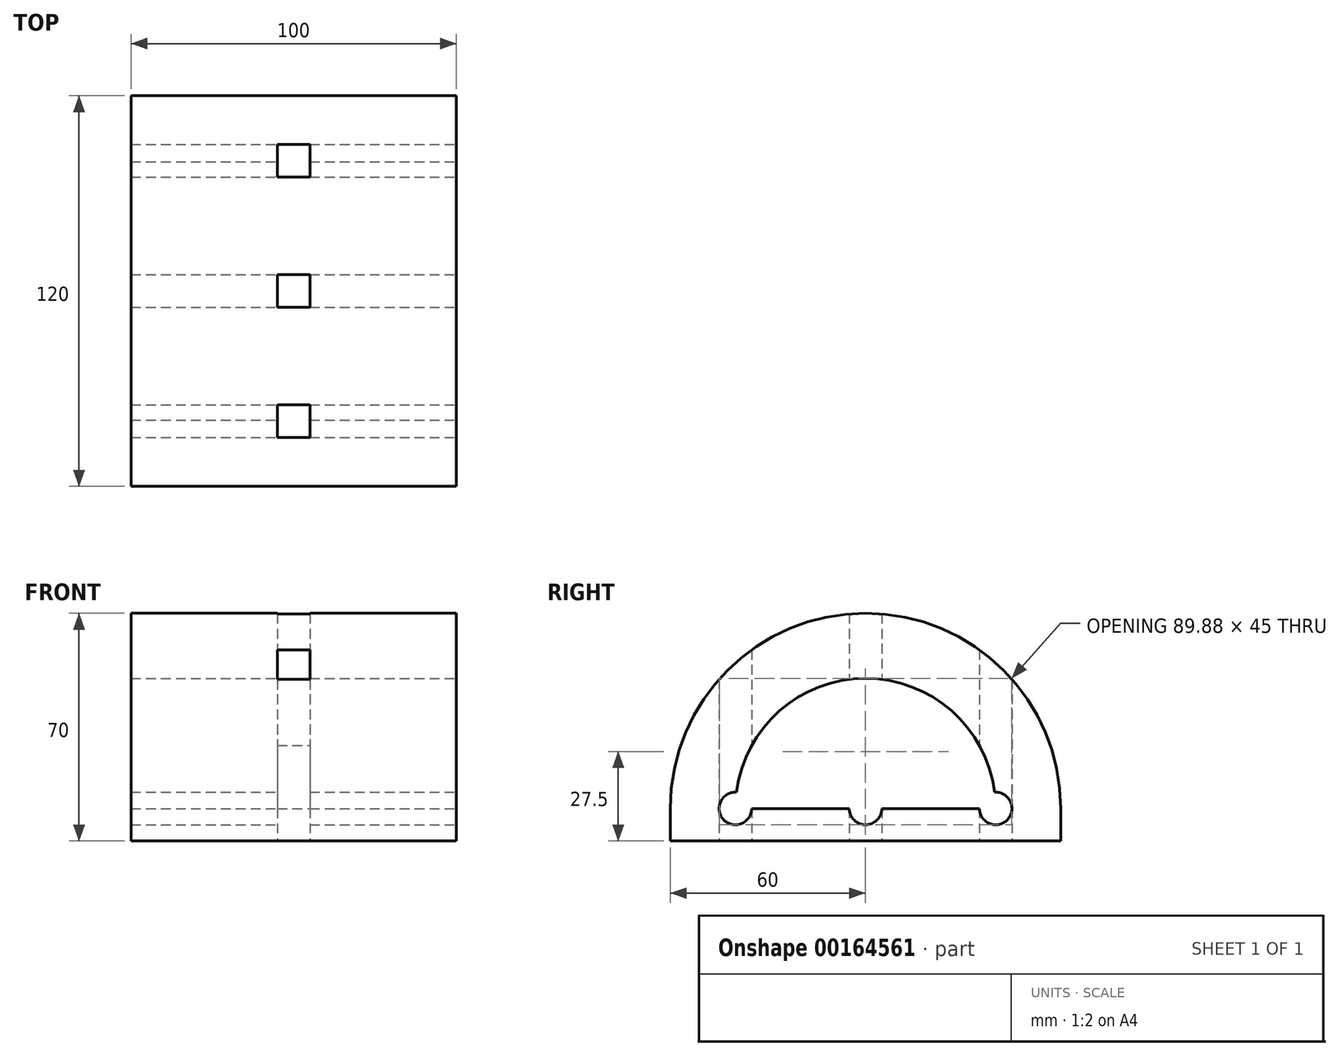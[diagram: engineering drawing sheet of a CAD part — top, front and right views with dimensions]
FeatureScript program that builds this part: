
annotation { "Feature Type Name" : "Feature", "Feature Type Description" : "" }
export const myFeature = defineFeature(function(context is Context, id is Id, definition is map)
    precondition{}
    {
        {
            var Q0;
            Q0=qCreatedBy(makeId("Right.planeOp"),FACE);
            var sketch = newSketch(context, id + "F0", { "sketchPlane" : qUnion([Q0])});
            skLineSegment(sketch, "E0.top", {"start": v(60, 10) * mm, "end": v(-60, 10) * mm});
            skLineSegment(sketch, "E0.left", {"start": v(60, 0) * mm, "end": v(60, 10) * mm});
            skLineSegment(sketch, "E0.right", {"start": v(-60, 0) * mm, "end": v(-60, 10) * mm});
            skPoint(sketch, "E0.middle", {"position": v(0, 0) * mm});
            skLineSegment(sketch, "E1", {"start": v(-60, 0) * mm, "end": v(60, 0) * mm});
            skArc(sketch, "E2", {"start": v(60, 10) * mm, "mid": v(0, 70) * mm, "end": v(-60, 10) * mm});
            skSolve(sketch);
        }
        {
            var Q0;
            Q0 = qSketchRegion(id + "F0", true);
            extrude(context, id + "F1", {"entities" : qUnion([Q0]), "depth" : 100 * mm});
        }
        {
            var Q0;
            Q0=makeQuery(id+"F1.opExtrude","CAP_FACE",FACE,{"disambiguationData":[OSD([sQuery(id+"F0.wireOp",EDGE,"E0.left"),sQuery(id+"F0.wireOp",EDGE,"E0.right"),sQuery(id+"F0.wireOp",EDGE,"E1"),sQuery(id+"F0.wireOp",EDGE,"E2")])],"isStart":false});
            var sketch = newSketch(context, id + "F2", { "sketchPlane" : qUnion([Q0])});
            skLineSegment(sketch, "E3", {"start": v(-40, 10) * mm, "end": v(40, 10) * mm});
            skArc(sketch, "E4", {"start": v(40, 10) * mm, "mid": v(0, 50) * mm, "end": v(-40, 10) * mm});
            skSolve(sketch);
        }
        {
            var Q0;
            Q0 = qSketchRegion(id + "F2", true);
            extrude(context, id + "F3", {"entities" : qUnion([Q0]), "operationType" : NewBodyOperationType.REMOVE, "endBound" : BoundingType.THROUGH_ALL, "oppositeDirection" : true, "depth" : 25 * mm});
        }
        {
            var Q0;
            Q0=makeQuery(id+"F1.opExtrude","CAP_FACE",FACE,{"disambiguationData":[OSD([sQuery(id+"F0.wireOp",EDGE,"E0.left"),sQuery(id+"F0.wireOp",EDGE,"E0.right"),sQuery(id+"F0.wireOp",EDGE,"E1"),sQuery(id+"F0.wireOp",EDGE,"E2")])],"isStart":false});
            var sketch = newSketch(context, id + "F4", { "sketchPlane" : qUnion([Q0])});
            skCircle(sketch, "E5", {"center": v(0, 10) * mm, "radius": 5 * mm});
            skCircle(sketch, "E6", {"center": v(40, 10) * mm, "radius": 5 * mm});
            skCircle(sketch, "E7", {"center": v(-40, 10) * mm, "radius": 5 * mm});
            skSolve(sketch);
        }
        {
            var Q0;
            {var subQ0=sQuery(id+"F4.wireOp",EDGE,"E5");var subQ1=makeQuery(id+"F3.boolean.opBoolean","COPY",EDGE,{"derivedFrom":makeQuery(id+"F3.opExtrude","CAP_EDGE",EDGE,{"disambiguationData":[OSD([sQuery(id+"F2.wireOp",EDGE,"E3")])],"isStart":true})});var subQ2=makeQuery(id+"F4.imprint","INTERSECT",VERTEX,{"disambiguationData":[OD(0.0)],"derivedFrom":[subQ1,subQ0]});Q0=makeQuery(id+"F4.imprint","IMPRINT",FACE,{"disambiguationData":[TD([[makeQuery(id+"F4.imprint","IMPRINT",EDGE,{"disambiguationData":[TD([[subQ2,-1.0]])],"derivedFrom":subQ0}),1.0]])]});}
            var Q1;
            {var subQ0=sQuery(id+"F4.wireOp",EDGE,"E5");var subQ1=makeQuery(id+"F3.boolean.opBoolean","COPY",EDGE,{"derivedFrom":makeQuery(id+"F3.opExtrude","CAP_EDGE",EDGE,{"disambiguationData":[OSD([sQuery(id+"F2.wireOp",EDGE,"E3")])],"isStart":true})});var subQ2=makeQuery(id+"F4.imprint","INTERSECT",VERTEX,{"disambiguationData":[OD(0.0)],"derivedFrom":[subQ1,subQ0]});Q1=makeQuery(id+"F4.imprint","IMPRINT",FACE,{"disambiguationData":[TD([[makeQuery(id+"F4.imprint","IMPRINT",EDGE,{"disambiguationData":[TD([[subQ2,1.0]])],"derivedFrom":subQ0}),1.0]])]});}
            var Q2;
            {var subQ0=sQuery(id+"F4.wireOp",EDGE,"E6");var subQ1=makeQuery(id+"F3.boolean.opBoolean","COPY",EDGE,{"derivedFrom":makeQuery(id+"F3.opExtrude","CAP_EDGE",EDGE,{"disambiguationData":[OSD([sQuery(id+"F2.wireOp",EDGE,"E4")])],"isStart":true})});var subQ2=makeQuery(id+"F4.imprint","INTERSECT",VERTEX,{"derivedFrom":[subQ1,subQ0]});Q2=makeQuery(id+"F4.imprint","IMPRINT",FACE,{"disambiguationData":[TD([[makeQuery(id+"F4.imprint","IMPRINT",EDGE,{"disambiguationData":[TD([[subQ2,1.0]])],"derivedFrom":subQ0}),1.0]])]});}
            var Q3;
            {var subQ0=sQuery(id+"F4.wireOp",EDGE,"E7");var subQ1=makeQuery(id+"F3.boolean.opBoolean","COPY",EDGE,{"derivedFrom":makeQuery(id+"F3.opExtrude","CAP_EDGE",EDGE,{"disambiguationData":[OSD([sQuery(id+"F2.wireOp",EDGE,"E4")])],"isStart":true})});var subQ2=makeQuery(id+"F4.imprint","INTERSECT",VERTEX,{"derivedFrom":[subQ1,subQ0]});Q3=makeQuery(id+"F4.imprint","IMPRINT",FACE,{"disambiguationData":[TD([[makeQuery(id+"F4.imprint","IMPRINT",EDGE,{"disambiguationData":[TD([[subQ2,-1.0]])],"derivedFrom":subQ0}),1.0]])]});}
            var Q4;
            {var subQ0=sQuery(id+"F4.wireOp",EDGE,"E7");var subQ1=makeQuery(id+"F3.boolean.opBoolean","COPY",EDGE,{"derivedFrom":makeQuery(id+"F3.opExtrude","CAP_EDGE",EDGE,{"disambiguationData":[OSD([sQuery(id+"F2.wireOp",EDGE,"E4")])],"isStart":true})});var subQ2=makeQuery(id+"F4.imprint","INTERSECT",VERTEX,{"derivedFrom":[subQ1,subQ0]});Q4=makeQuery(id+"F4.imprint","IMPRINT",FACE,{"disambiguationData":[TD([[makeQuery(id+"F4.imprint","IMPRINT",EDGE,{"disambiguationData":[TD([[subQ2,1.0]])],"derivedFrom":subQ0}),1.0]])]});}
            var Q5;
            {var subQ0=sQuery(id+"F4.wireOp",EDGE,"E6");var subQ1=makeQuery(id+"F3.boolean.opBoolean","COPY",EDGE,{"derivedFrom":makeQuery(id+"F3.opExtrude","CAP_EDGE",EDGE,{"disambiguationData":[OSD([sQuery(id+"F2.wireOp",EDGE,"E4")])],"isStart":true})});var subQ2=makeQuery(id+"F4.imprint","INTERSECT",VERTEX,{"derivedFrom":[subQ1,subQ0]});Q5=makeQuery(id+"F4.imprint","IMPRINT",FACE,{"disambiguationData":[TD([[makeQuery(id+"F4.imprint","IMPRINT",EDGE,{"disambiguationData":[TD([[subQ2,-1.0]])],"derivedFrom":subQ0}),1.0]])]});}
            extrude(context, id + "F5", {"entities" : qUnion([Q0, Q1, Q2, Q3, Q4, Q5]), "operationType" : NewBodyOperationType.REMOVE, "endBound" : BoundingType.THROUGH_ALL, "oppositeDirection" : true, "depth" : 25 * mm});
        }
        {
            var Q0;
            Q0=makeQuery(id+"F1.opExtrude","SWEPT_FACE",FACE,{"disambiguationData":[OSD([sQuery(id+"F0.wireOp",EDGE,"E1")])]});
            var sketch = newSketch(context, id + "F6", { "sketchPlane" : qUnion([Q0])});
            skLineSegment(sketch, "E8.bottom", {"start": v(55, 5) * mm, "end": v(45, 5) * mm});
            skLineSegment(sketch, "E8.top", {"start": v(55, -5) * mm, "end": v(45, -5) * mm});
            skLineSegment(sketch, "E8.left", {"start": v(55, 5) * mm, "end": v(55, -5) * mm});
            skLineSegment(sketch, "E8.right", {"start": v(45, 5) * mm, "end": v(45, -5) * mm});
            skPoint(sketch, "E8.middle", {"position": v(50, 0) * mm});
            skLineSegment(sketch, "E9.bottom", {"start": v(55, 45) * mm, "end": v(45, 45) * mm});
            skLineSegment(sketch, "E9.top", {"start": v(55, 35) * mm, "end": v(45, 35) * mm});
            skLineSegment(sketch, "E9.left", {"start": v(55, 45) * mm, "end": v(55, 35) * mm});
            skLineSegment(sketch, "E9.right", {"start": v(45, 45) * mm, "end": v(45, 35) * mm});
            skPoint(sketch, "E9.middle", {"position": v(50, 40) * mm});
            skLineSegment(sketch, "E10.bottom", {"start": v(55, -35) * mm, "end": v(45, -35) * mm});
            skLineSegment(sketch, "E10.top", {"start": v(55, -45) * mm, "end": v(45, -45) * mm});
            skLineSegment(sketch, "E10.left", {"start": v(55, -35) * mm, "end": v(55, -45) * mm});
            skLineSegment(sketch, "E10.right", {"start": v(45, -35) * mm, "end": v(45, -45) * mm});
            skPoint(sketch, "E10.middle", {"position": v(50, -40) * mm});
            skSolve(sketch);
        }
        {
            var Q0;
            Q0=makeQuery(id+"F6.imprint","IMPRINT",FACE,{"disambiguationData":[TD([[makeQuery(id+"F6.imprint","IMPRINT",EDGE,{"derivedFrom":sQuery(id+"F6.wireOp",EDGE,"E9.bottom")}),1.0]])]});
            var Q1;
            Q1=makeQuery(id+"F6.imprint","IMPRINT",FACE,{"disambiguationData":[TD([[makeQuery(id+"F6.imprint","IMPRINT",EDGE,{"derivedFrom":sQuery(id+"F6.wireOp",EDGE,"E8.bottom")}),1.0]])]});
            var Q2;
            Q2=makeQuery(id+"F6.imprint","IMPRINT",FACE,{"disambiguationData":[TD([[makeQuery(id+"F6.imprint","IMPRINT",EDGE,{"derivedFrom":sQuery(id+"F6.wireOp",EDGE,"E10.bottom")}),1.0]])]});
            extrude(context, id + "F7", {"entities" : qUnion([Q0, Q1, Q2]), "operationType" : NewBodyOperationType.REMOVE, "endBound" : BoundingType.THROUGH_ALL, "oppositeDirection" : true, "depth" : 25 * mm});
        }
    });
